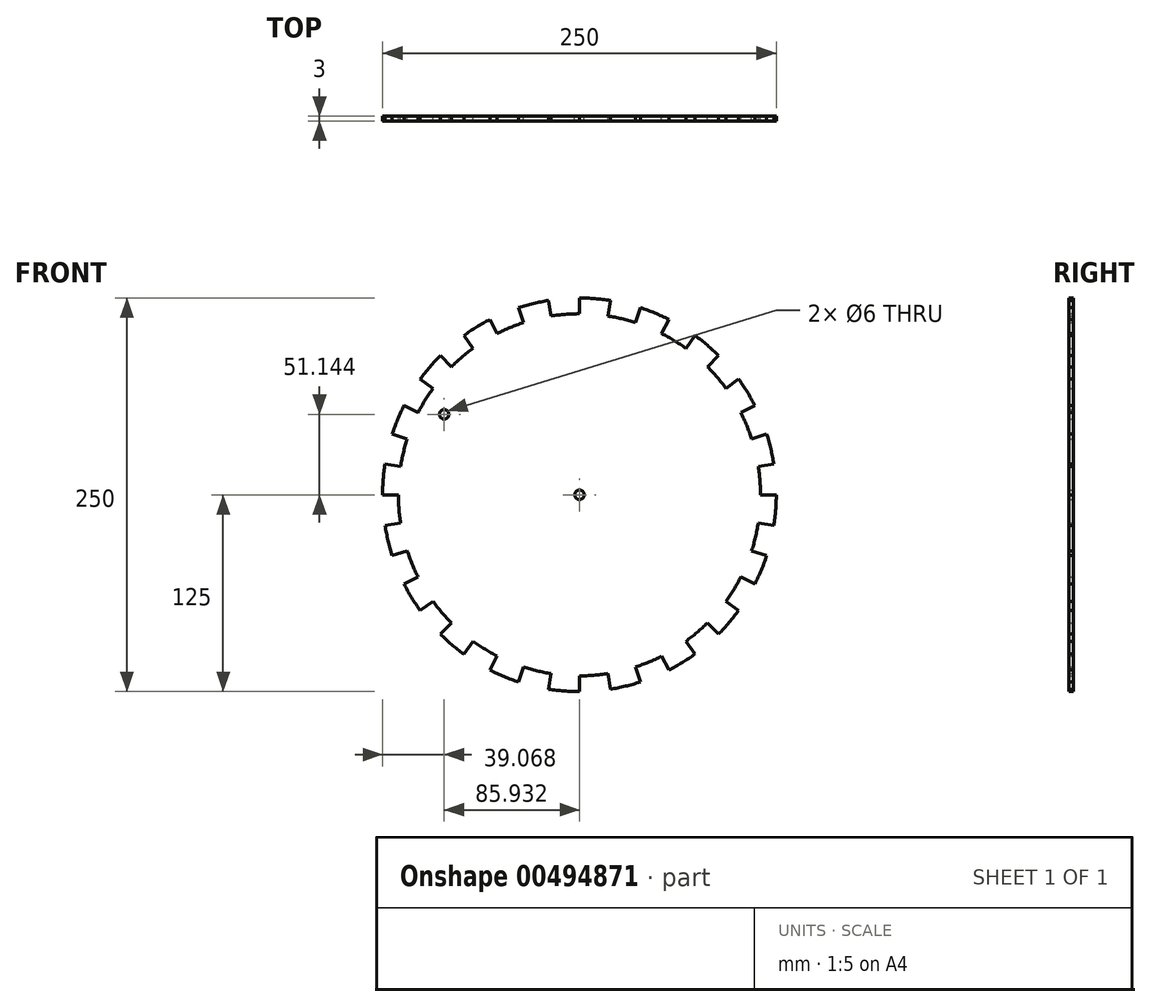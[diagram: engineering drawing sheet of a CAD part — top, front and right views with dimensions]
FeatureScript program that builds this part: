
annotation { "Feature Type Name" : "Feature", "Feature Type Description" : "" }
export const myFeature = defineFeature(function(context is Context, id is Id, definition is map)
    precondition{}
    {
        {
            var Q0;
            Q0=qCreatedBy(makeId("Front.planeOp"),FACE);
            var sketch = newSketch(context, id + "F0", { "sketchPlane" : qUnion([Q0])});
            skArc(sketch, "E0", {"start": v(19.55, 123.46) * mm, "mid": v(9.8, 124.61) * mm, "end": v(0, 125) * mm});
            skCircle(sketch, "E1", {"center": v(0, 0) * mm, "radius": 3 * mm});
            skCircle(sketch, "E2", {"center": v(-85.93, 51.14) * mm, "radius": 3 * mm});
            skArc(sketch, "E3", {"start": v(0, 115) * mm, "mid": v(-9.02, 114.65) * mm, "end": v(-17.99, 113.58) * mm});
            skLineSegment(sketch, "E4", {"start": v(0, 0) * mm, "end": v(0, 3) * mm});
            skLineSegment(sketch, "E5", {"start": v(0, 0) * mm, "end": v(0.47, 2.96) * mm});
            skLineSegment(sketch, "E6.trimOffspring", {"start": v(17.99, 113.58) * mm, "end": v(19.55, 123.46) * mm});
            skLineSegment(sketch, "E7.trimOffspring", {"start": v(0, 115) * mm, "end": v(0, 125) * mm});
            skLineSegment(sketch, "E8.1.0", {"start": v(-17.99, 113.58) * mm, "end": v(-19.55, 123.46) * mm});
            skLineSegment(sketch, "E8.1.1", {"start": v(-35.54, 109.37) * mm, "end": v(-38.63, 118.88) * mm});
            skArc(sketch, "E8.1.2", {"start": v(-19.55, 123.46) * mm, "mid": v(-29.18, 121.55) * mm, "end": v(-38.63, 118.88) * mm});
            skLineSegment(sketch, "E8.2.0", {"start": v(-52.2, 102.47) * mm, "end": v(-56.75, 111.38) * mm});
            skLineSegment(sketch, "E8.2.1", {"start": v(-67.6, 93.04) * mm, "end": v(-73.47, 101.13) * mm});
            skArc(sketch, "E8.2.2", {"start": v(-56.75, 111.38) * mm, "mid": v(-65.31, 106.58) * mm, "end": v(-73.47, 101.13) * mm});
            skLineSegment(sketch, "E8.3.0", {"start": v(-81.32, 81.32) * mm, "end": v(-88.39, 88.39) * mm});
            skLineSegment(sketch, "E8.3.1", {"start": v(-93.04, 67.6) * mm, "end": v(-101.13, 73.47) * mm});
            skArc(sketch, "E8.3.2", {"start": v(-88.39, 88.39) * mm, "mid": v(-95.05, 81.18) * mm, "end": v(-101.13, 73.47) * mm});
            skLineSegment(sketch, "E8.4.0", {"start": v(-102.47, 52.2) * mm, "end": v(-111.38, 56.75) * mm});
            skLineSegment(sketch, "E8.4.1", {"start": v(-109.37, 35.54) * mm, "end": v(-118.88, 38.63) * mm});
            skArc(sketch, "E8.4.2", {"start": v(-111.38, 56.75) * mm, "mid": v(-115.48, 47.84) * mm, "end": v(-118.88, 38.63) * mm});
            skLineSegment(sketch, "E8.5.0", {"start": v(-113.58, 17.99) * mm, "end": v(-123.46, 19.55) * mm});
            skLineSegment(sketch, "E8.5.1", {"start": v(-115, 0) * mm, "end": v(-125, 0) * mm});
            skArc(sketch, "E8.5.2", {"start": v(-123.46, 19.55) * mm, "mid": v(-124.61, 9.8) * mm, "end": v(-125, 0) * mm});
            skLineSegment(sketch, "E8.6.0", {"start": v(-113.58, -17.99) * mm, "end": v(-123.46, -19.55) * mm});
            skLineSegment(sketch, "E8.6.1", {"start": v(-109.37, -35.54) * mm, "end": v(-118.88, -38.63) * mm});
            skArc(sketch, "E8.6.2", {"start": v(-123.46, -19.55) * mm, "mid": v(-121.55, -29.18) * mm, "end": v(-118.88, -38.63) * mm});
            skLineSegment(sketch, "E8.7.0", {"start": v(-102.47, -52.2) * mm, "end": v(-111.38, -56.75) * mm});
            skLineSegment(sketch, "E8.7.1", {"start": v(-93.04, -67.6) * mm, "end": v(-101.13, -73.47) * mm});
            skArc(sketch, "E8.7.2", {"start": v(-111.38, -56.75) * mm, "mid": v(-106.58, -65.31) * mm, "end": v(-101.13, -73.47) * mm});
            skLineSegment(sketch, "E8.8.0", {"start": v(-81.32, -81.32) * mm, "end": v(-88.39, -88.39) * mm});
            skLineSegment(sketch, "E8.8.1", {"start": v(-67.6, -93.04) * mm, "end": v(-73.47, -101.13) * mm});
            skArc(sketch, "E8.8.2", {"start": v(-88.39, -88.39) * mm, "mid": v(-81.18, -95.05) * mm, "end": v(-73.47, -101.13) * mm});
            skLineSegment(sketch, "E8.9.0", {"start": v(-52.2, -102.47) * mm, "end": v(-56.75, -111.38) * mm});
            skLineSegment(sketch, "E8.9.1", {"start": v(-35.54, -109.37) * mm, "end": v(-38.63, -118.88) * mm});
            skArc(sketch, "E8.9.2", {"start": v(-56.75, -111.38) * mm, "mid": v(-47.84, -115.48) * mm, "end": v(-38.63, -118.88) * mm});
            skLineSegment(sketch, "E8.10.0", {"start": v(-17.99, -113.58) * mm, "end": v(-19.55, -123.46) * mm});
            skLineSegment(sketch, "E8.10.1", {"start": v(0, -115) * mm, "end": v(0, -125) * mm});
            skArc(sketch, "E8.10.2", {"start": v(-19.55, -123.46) * mm, "mid": v(-9.8, -124.61) * mm, "end": v(0, -125) * mm});
            skLineSegment(sketch, "E8.11.0", {"start": v(17.99, -113.58) * mm, "end": v(19.55, -123.46) * mm});
            skLineSegment(sketch, "E8.11.1", {"start": v(35.54, -109.37) * mm, "end": v(38.63, -118.88) * mm});
            skArc(sketch, "E8.11.2", {"start": v(19.55, -123.46) * mm, "mid": v(29.18, -121.55) * mm, "end": v(38.63, -118.88) * mm});
            skLineSegment(sketch, "E8.12.0", {"start": v(52.2, -102.47) * mm, "end": v(56.75, -111.38) * mm});
            skLineSegment(sketch, "E8.12.1", {"start": v(67.6, -93.04) * mm, "end": v(73.47, -101.13) * mm});
            skArc(sketch, "E8.12.2", {"start": v(56.75, -111.38) * mm, "mid": v(65.31, -106.58) * mm, "end": v(73.47, -101.13) * mm});
            skLineSegment(sketch, "E8.13.0", {"start": v(81.32, -81.32) * mm, "end": v(88.39, -88.39) * mm});
            skLineSegment(sketch, "E8.13.1", {"start": v(93.04, -67.6) * mm, "end": v(101.13, -73.47) * mm});
            skArc(sketch, "E8.13.2", {"start": v(88.39, -88.39) * mm, "mid": v(95.05, -81.18) * mm, "end": v(101.13, -73.47) * mm});
            skLineSegment(sketch, "E8.14.0", {"start": v(102.47, -52.2) * mm, "end": v(111.38, -56.75) * mm});
            skLineSegment(sketch, "E8.14.1", {"start": v(109.37, -35.54) * mm, "end": v(118.88, -38.63) * mm});
            skArc(sketch, "E8.14.2", {"start": v(111.38, -56.75) * mm, "mid": v(115.48, -47.84) * mm, "end": v(118.88, -38.63) * mm});
            skLineSegment(sketch, "E8.15.0", {"start": v(113.58, -17.99) * mm, "end": v(123.46, -19.55) * mm});
            skLineSegment(sketch, "E8.15.1", {"start": v(115, 0) * mm, "end": v(125, 0) * mm});
            skArc(sketch, "E8.15.2", {"start": v(123.46, -19.55) * mm, "mid": v(124.61, -9.8) * mm, "end": v(125, 0) * mm});
            skLineSegment(sketch, "E8.16.0", {"start": v(113.58, 17.99) * mm, "end": v(123.46, 19.55) * mm});
            skLineSegment(sketch, "E8.16.1", {"start": v(109.37, 35.54) * mm, "end": v(118.88, 38.63) * mm});
            skArc(sketch, "E8.16.2", {"start": v(123.46, 19.55) * mm, "mid": v(121.55, 29.18) * mm, "end": v(118.88, 38.63) * mm});
            skLineSegment(sketch, "E8.17.0", {"start": v(102.47, 52.2) * mm, "end": v(111.38, 56.75) * mm});
            skLineSegment(sketch, "E8.17.1", {"start": v(93.04, 67.6) * mm, "end": v(101.13, 73.47) * mm});
            skArc(sketch, "E8.17.2", {"start": v(111.38, 56.75) * mm, "mid": v(106.58, 65.31) * mm, "end": v(101.13, 73.47) * mm});
            skLineSegment(sketch, "E8.18.0", {"start": v(81.32, 81.32) * mm, "end": v(88.39, 88.39) * mm});
            skLineSegment(sketch, "E8.18.1", {"start": v(67.6, 93.04) * mm, "end": v(73.47, 101.13) * mm});
            skArc(sketch, "E8.18.2", {"start": v(88.39, 88.39) * mm, "mid": v(81.18, 95.05) * mm, "end": v(73.47, 101.13) * mm});
            skLineSegment(sketch, "E8.19.0", {"start": v(52.2, 102.47) * mm, "end": v(56.75, 111.38) * mm});
            skLineSegment(sketch, "E8.19.1", {"start": v(35.54, 109.37) * mm, "end": v(38.63, 118.88) * mm});
            skArc(sketch, "E8.19.2", {"start": v(56.75, 111.38) * mm, "mid": v(47.84, 115.48) * mm, "end": v(38.63, 118.88) * mm});
            skArc(sketch, "E9.trimOffspring", {"start": v(-35.54, 109.37) * mm, "mid": v(-44, 106.25) * mm, "end": v(-52.2, 102.47) * mm});
            skArc(sketch, "E10.trimOffspring", {"start": v(-67.6, 93.04) * mm, "mid": v(-74.69, 87.45) * mm, "end": v(-81.32, 81.32) * mm});
            skArc(sketch, "E11.trimOffspring", {"start": v(-93.04, 67.6) * mm, "mid": v(26.85, -111.82) * mm, "end": v(52.2, 102.47) * mm});
            skArc(sketch, "E12.trimOffspring", {"start": v(35.54, 109.37) * mm, "mid": v(26.85, 111.82) * mm, "end": v(17.99, 113.58) * mm});
            skSolve(sketch);
        }
        {
            var Q0;
            Q0 = qSketchRegion(id + "F0", true);
            extrude(context, id + "F1", {"entities" : qUnion([Q0]), "depth" : 3 * mm});
        }
    });
